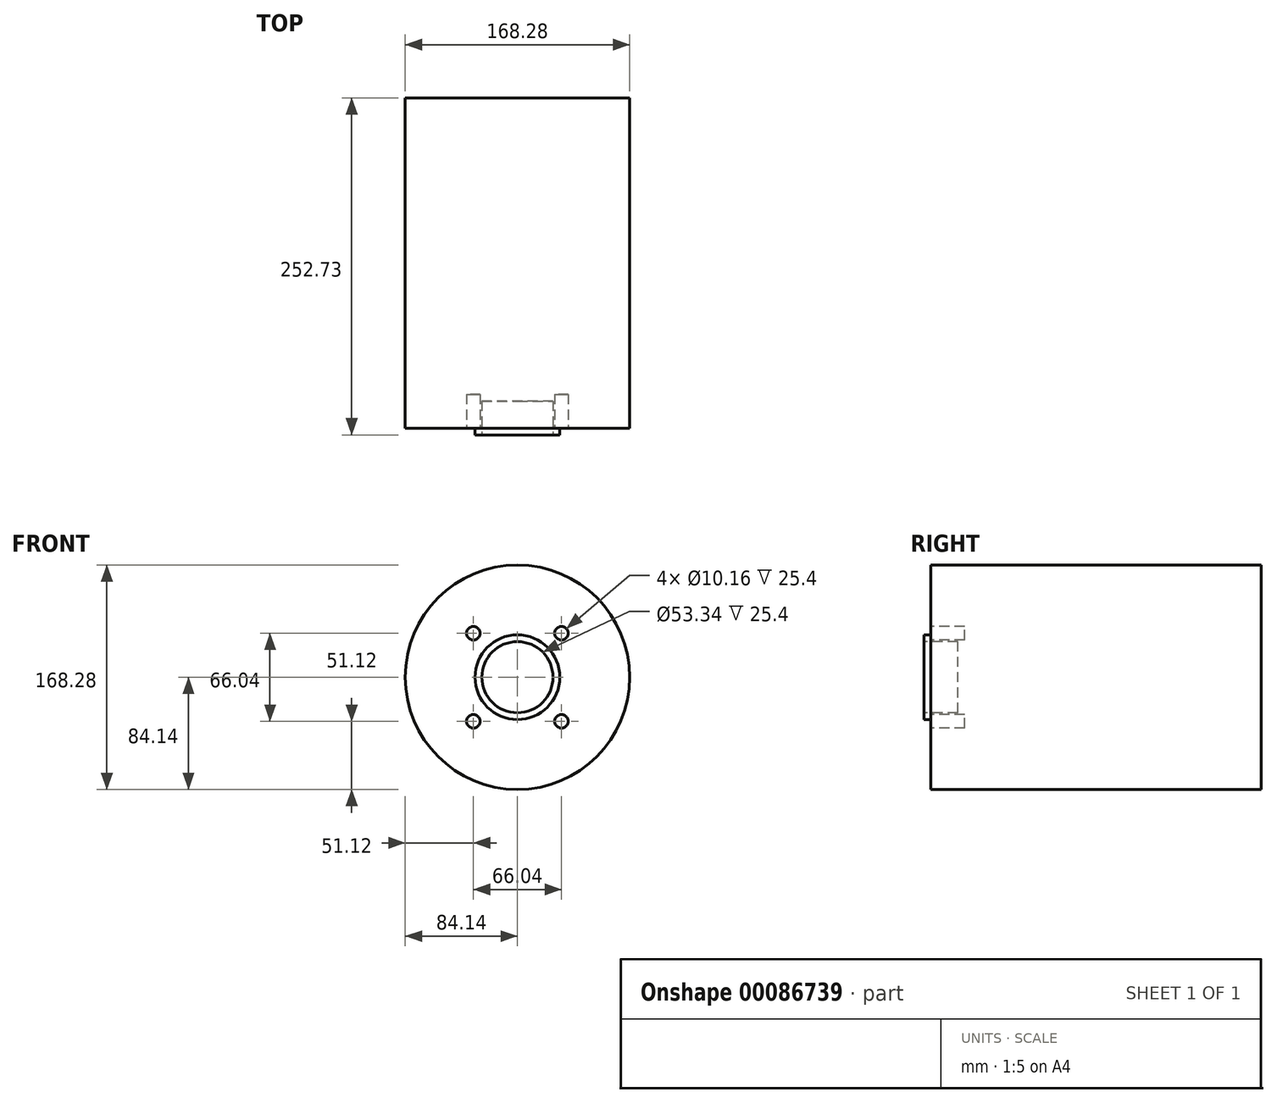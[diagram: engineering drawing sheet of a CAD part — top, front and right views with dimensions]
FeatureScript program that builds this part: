
annotation { "Feature Type Name" : "Feature", "Feature Type Description" : "" }
export const myFeature = defineFeature(function(context is Context, id is Id, definition is map)
    precondition{}
    {
        {
            var Q0;
            Q0=qCreatedBy(makeId("Front.planeOp"),FACE);
            var sketch = newSketch(context, id + "F0", { "sketchPlane" : qUnion([Q0])});
            skCircle(sketch, "E0", {"center": v(0, 0) * mm, "radius": 84.14 * mm});
            skSolve(sketch);
        }
        {
            var Q0;
            Q0=makeQuery(id+"F0.imprint","IMPRINT",FACE,{"disambiguationData":[TD([[makeQuery(id+"F0.imprint","IMPRINT",EDGE,{"derivedFrom":sQuery(id+"F0.wireOp",EDGE,"E0")}),1.0]])]});
            var Q1;
            Q1=qSketchRegion(id+"F2",true);
            extrude(context, id + "F1", {"entities" : qUnion([Q0, Q1]), "depth" : 247.65 * mm});
        }
        {
            var Q0;
            Q0=makeQuery(id+"F1.opExtrude","CAP_FACE",FACE,{"disambiguationData":[OSD([sQuery(id+"F0.wireOp",EDGE,"E0")])],"isStart":false});
            var sketch = newSketch(context, id + "F2", { "sketchPlane" : qUnion([Q0])});
            skCircle(sketch, "E1", {"center": v(0, 0) * mm, "radius": 31.75 * mm});
            skSolve(sketch);
        }
        {
            var Q0;
            Q0=makeQuery(id+"F2.imprint","IMPRINT",FACE,{"disambiguationData":[TD([[makeQuery(id+"F2.imprint","IMPRINT",EDGE,{"derivedFrom":sQuery(id+"F2.wireOp",EDGE,"E1")}),1.0]])]});
            extrude(context, id + "F3", {"entities" : qUnion([Q0]), "operationType" : NewBodyOperationType.ADD, "depth" : 5.08 * mm});
        }
        {
            var Q0;
            Q0=makeQuery(id+"F1.opExtrude","CAP_FACE",FACE,{"disambiguationData":[OSD([sQuery(id+"F0.wireOp",EDGE,"E0")])],"isStart":false});
            var sketch = newSketch(context, id + "F4", { "sketchPlane" : qUnion([Q0])});
            skLineSegment(sketch, "E2.bottom", {"start": v(-38.1, 38.1) * mm, "end": v(38.1, 38.1) * mm});
            skLineSegment(sketch, "E2.top", {"start": v(-38.1, -38.1) * mm, "end": v(38.1, -38.1) * mm});
            skLineSegment(sketch, "E2.left", {"start": v(-38.1, 38.1) * mm, "end": v(-38.1, -38.1) * mm});
            skLineSegment(sketch, "E2.right", {"start": v(38.1, 38.1) * mm, "end": v(38.1, -38.1) * mm});
            skPoint(sketch, "E2.middle", {"position": v(0, 0) * mm});
            skCircle(sketch, "E3", {"center": v(33.02, 33.02) * mm, "radius": 5.08 * mm});
            skCircle(sketch, "E4.1.0", {"center": v(-33.02, 33.02) * mm, "radius": 5.08 * mm});
            skCircle(sketch, "E4.2.0", {"center": v(-33.02, -33.02) * mm, "radius": 5.08 * mm});
            skCircle(sketch, "E4.3.0", {"center": v(33.02, -33.02) * mm, "radius": 5.08 * mm});
            skSolve(sketch);
        }
        {
            var Q0;
            {var subQ0=sQuery(id+"F4.wireOp",EDGE,"E4.1.0");var subQ1=makeQuery(id+"F4.imprint","INTERSECT",VERTEX,{"derivedFrom":[sQuery(id+"F4.wireOp",EDGE,"E2.bottom"),subQ0]});Q0=makeQuery(id+"F4.imprint","IMPRINT",FACE,{"disambiguationData":[TD([[makeQuery(id+"F4.imprint","IMPRINT",EDGE,{"disambiguationData":[TD([[subQ1,-1.0]])],"derivedFrom":subQ0}),1.0]])]});}
            var Q1;
            {var subQ0=sQuery(id+"F4.wireOp",EDGE,"E3");var subQ1=makeQuery(id+"F4.imprint","INTERSECT",VERTEX,{"derivedFrom":[sQuery(id+"F4.wireOp",EDGE,"E2.bottom"),subQ0]});Q1=makeQuery(id+"F4.imprint","IMPRINT",FACE,{"disambiguationData":[TD([[makeQuery(id+"F4.imprint","IMPRINT",EDGE,{"disambiguationData":[TD([[subQ1,1.0]])],"derivedFrom":subQ0}),1.0]])]});}
            var Q2;
            {var subQ0=sQuery(id+"F4.wireOp",EDGE,"E4.3.0");var subQ1=makeQuery(id+"F4.imprint","INTERSECT",VERTEX,{"derivedFrom":[sQuery(id+"F4.wireOp",EDGE,"E2.top"),subQ0]});Q2=makeQuery(id+"F4.imprint","IMPRINT",FACE,{"disambiguationData":[TD([[makeQuery(id+"F4.imprint","IMPRINT",EDGE,{"disambiguationData":[TD([[subQ1,-1.0]])],"derivedFrom":subQ0}),1.0]])]});}
            var Q3;
            {var subQ0=sQuery(id+"F4.wireOp",EDGE,"E4.2.0");var subQ1=makeQuery(id+"F4.imprint","INTERSECT",VERTEX,{"derivedFrom":[sQuery(id+"F4.wireOp",EDGE,"E2.top"),subQ0]});Q3=makeQuery(id+"F4.imprint","IMPRINT",FACE,{"disambiguationData":[TD([[makeQuery(id+"F4.imprint","IMPRINT",EDGE,{"disambiguationData":[TD([[subQ1,1.0]])],"derivedFrom":subQ0}),1.0]])]});}
            extrude(context, id + "F5", {"entities" : qUnion([Q0, Q1, Q2, Q3]), "operationType" : NewBodyOperationType.REMOVE, "oppositeDirection" : true, "depth" : 25.4 * mm});
        }
        {
            var Q0;
            Q0=makeQuery(id+"F3.opExtrude","CAP_FACE",FACE,{"disambiguationData":[OSD([sQuery(id+"F2.wireOp",EDGE,"E1")])],"isStart":false});
            var sketch = newSketch(context, id + "F6", { "sketchPlane" : qUnion([Q0])});
            skCircle(sketch, "E5", {"center": v(0, 0) * mm, "radius": 26.67 * mm});
            skSolve(sketch);
        }
        {
            var Q0;
            Q0=makeQuery(id+"F6.imprint","IMPRINT",FACE,{"disambiguationData":[TD([[makeQuery(id+"F6.imprint","IMPRINT",EDGE,{"derivedFrom":sQuery(id+"F6.wireOp",EDGE,"E5")}),1.0]])]});
            extrude(context, id + "F7", {"entities" : qUnion([Q0]), "operationType" : NewBodyOperationType.REMOVE, "oppositeDirection" : true, "depth" : 25.4 * mm});
        }
    });
